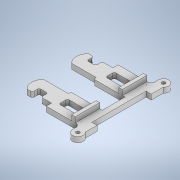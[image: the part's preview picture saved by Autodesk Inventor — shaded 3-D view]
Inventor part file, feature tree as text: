
AUTODESK INVENTOR PART (.ipt)
format: ipt  version: 2022 (Build 260153000, 153)  size: 294,400 bytes
history: native  units: in
note: dims shown in document units (in); Inventor stores cm internally (conversion verified against a paired STEP export)
features: extrude x5, sketch x5, mirror x3
ambient origin geometry x8: Origin, YZ Plane, XZ Plane, XY Plane, X Axis, Y Axis, Z Axis, Center Point
bodies: Solid1 (feature_tree)
feature tree (13):
  extrude  "Extrusion1"  TaperAngle=0.0deg  [1 undecoded]
  mirror  "Mirror1"
  extrude  "Extrusion2"  Depth=0.1969in
  mirror  "Mirror2"
  extrude  "Extrusion3"  Depth=0.1378in
  extrude  "Extrusion4"  Depth=0.0787in
  extrude  "Extrusion5"  Depth=0.0787in
  mirror  "Mirror3"
  sketch  "Sketch1"  dims[d1=0.8071in d2=0.0in]
  sketch  "Sketch2"  dims[d3=0.4724in d4=0.1969in]
  sketch  "Sketch3"  dims[d5=0.1832in d6=0.1378in]
  sketch  "Sketch5"  dims[d7=0.0787in d8=0.0787in]
  sketch  "Sketch6"  dims[d9=0.0787in d10=0.0787in d11=0.0394in d12=0.0394in d13=0.0394in d14=0.0394in d15=0.0394in d16=0.0394in d17=0.0394in d18=0.0394in d19=0.1575in d20=0.0787in d21=0.563in d22=0.7087in d23=0.1181in d24=0.374in d25=0.3765in d26=0.5118in d27=0.0709in d28=0.1969in d29=0.3346in d30=0.0787in d31=0.0787in d32=0.0787in d33=0.0787in d34=0.0394in d35=0.0394in d36=0.0394in d37=0.0394in d38=0.0394in d39=0.0394in d40=0.0394in d41=0.0394in d42=0.1181in d43=0.0in d44=0.0787in d46=0.1575in d47=0.2362in d48=0.2362in d49=0.1575in d50=0.0787in d51=0.2441in d52=0.1181in d53=0.0in d54=1.2205in d55=0.0in d56=0.6102in d57=0.1181in d58=0.1181in d59=0.0in d60=0.5118in d61=0.2559in d62=0.1181in d63=0.0in d64=0.9646in d65=0.0591in d66=0.0in d67=0.1181in d68=0.0in]
note: 1 required parameter value undecoded (feature->parameter linkage not recoverable at this tier; creation-order binding heuristic only, values carry confidence <= 0.55)
